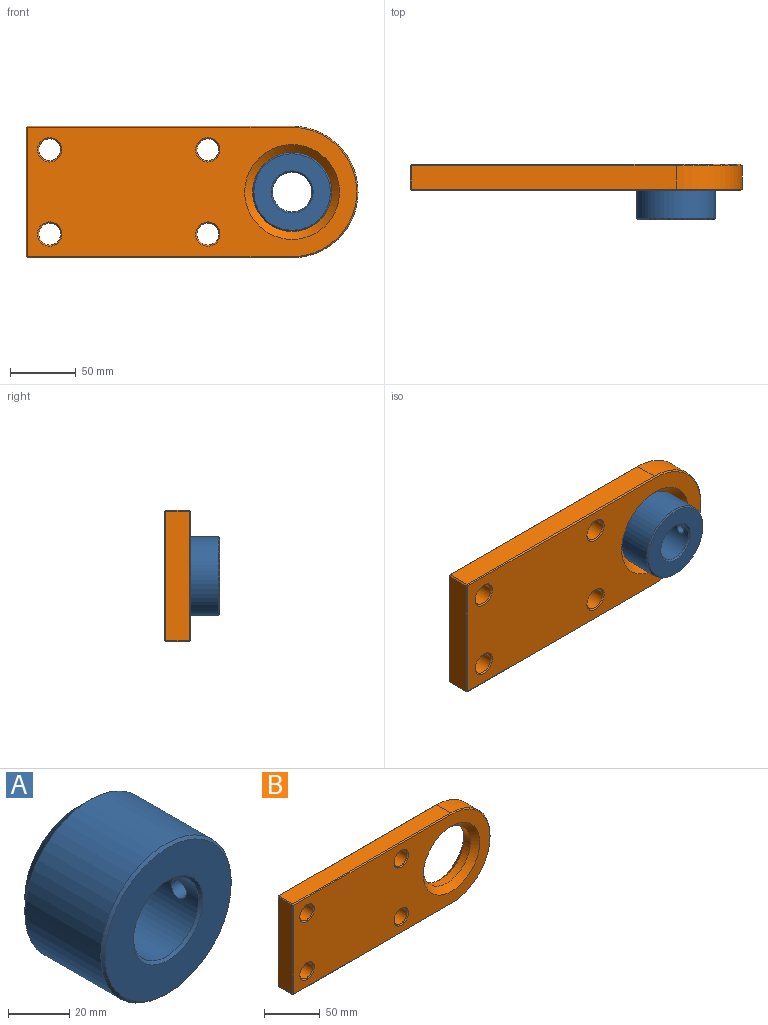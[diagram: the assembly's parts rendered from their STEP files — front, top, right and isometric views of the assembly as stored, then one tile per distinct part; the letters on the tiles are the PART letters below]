
ASSEMBLY  parts=2 mates=1
PART A: 10 faces, bbox 60x42x60 mm
  f0: cylinder r=15mm len=40mm, axis (0,1,0), area 3733.2mm2, adj f4,f6,f8
  f1: cylinder r=30mm len=60mm, axis (0,1,0), area 6538.5mm2, adj f5,f7,f9
  f2: plane 58x58mm, normal (0,-1,0), area 1837.8mm2, adj f4,f5
  f3: plane 48x48mm, normal (0,1,0), area 1005.3mm2, adj f6,f7
  f4: cone r=15mm half-angle=45deg, axis (0,-1,0), area 137.7mm2, adj f0,f2
  f5: cone r=29mm half-angle=45deg, axis (0,1,0), area 262.1mm2, adj f1,f2
  f6: cone r=16mm half-angle=45deg, axis (0,1,0), area 137.7mm2, adj f0,f3
  f7: cone r=30mm half-angle=45deg, axis (0,-1,0), area 1439.5mm2, adj f1,f3
  f8: cylinder r=3.4mm len=14.18mm, axis (-1,0,0), area 302.9mm2, adj f0,f9
  f9: bspline ~8.85x8.59mm, area 31.9mm2, adj f1,f8
PART B: 35 faces, bbox 252x20x100 mm
  f0: cylinder r=50mm len=100mm, axis (0,1,0), area 2827.4mm2, adj f1,f8,f13,f26
  f1: plane 201x18mm, normal (0,0,1), area 3618mm2, adj f0,f15,f20,f25
  f2: plane 98x18mm, normal (-1,0,0), area 1764mm2, adj f16,f19,f20,f21
  f3: cylinder r=8.25mm len=18mm, axis (0,1,0), area 933.1mm2, adj f29,f33
  f4: cylinder r=8.25mm len=18mm, axis (0,1,0), area 933.1mm2, adj f30,f34
  f5: cylinder r=8.25mm len=18mm, axis (0,1,0), area 933.1mm2, adj f28,f32
  f6: cylinder r=8.25mm len=18mm, axis (0,1,0), area 933.1mm2, adj f27,f31
  f7: cylinder r=30mm len=60mm, axis (0,1,0), area 1508mm2, adj f11,f12
  f8: plane 201x18mm, normal (0,0,-1), area 3618mm2, adj f0,f14,f19,f24
  f9: plane 250x98mm, normal (0,-1,0), area 18322.8mm2, adj f12,f13,f14,f15,f16,f31,f32,f33
  f10: plane 250x98mm, normal (0,1,0), area 18322.8mm2, adj f11,f21,f24,f25,f26,f27,f28,f29
  f11: cone r=36mm half-angle=45deg, axis (0,1,0), area 1759.4mm2, adj f7,f10
  f12: cone r=30mm half-angle=45deg, axis (0,-1,0), area 1759.4mm2, adj f7,f9
  f13: cone r=49mm half-angle=45deg, axis (0,1,0), area 219.9mm2, adj f0,f9,f14,f15
  f14: plane 201x1mm, normal (0,-0.71,-0.71), area 284.3mm2, adj f8,f9,f13,f17
  f15: plane 201x1mm, normal (0,-0.71,0.71), area 284.3mm2, adj f1,f9,f13,f18
  f16: plane 98x1mm, normal (-0.71,-0.71,0), area 138.6mm2, adj f2,f9,f17,f18
  f17: plane 1x1mm, normal (-0.58,-0.58,-0.58), area 0.9mm2, adj f14,f16,f19
  f18: plane 1x1mm, normal (-0.58,-0.58,0.58), area 0.9mm2, adj f15,f16,f20
  f19: plane 18x1mm, normal (-0.71,0,-0.71), area 25.5mm2, adj f2,f8,f17,f22
  f20: plane 18x1mm, normal (-0.71,0,0.71), area 25.5mm2, adj f1,f2,f18,f23
  f21: plane 98x1mm, normal (-0.71,0.71,0), area 138.6mm2, adj f2,f10,f22,f23
  f22: plane 1x1mm, normal (-0.58,0.58,-0.58), area 0.9mm2, adj f19,f21,f24
  f23: plane 1x1mm, normal (-0.58,0.58,0.58), area 0.9mm2, adj f20,f21,f25
  f24: plane 201x1mm, normal (0,0.71,-0.71), area 284.3mm2, adj f8,f10,f22,f26
  f25: plane 201x1mm, normal (0,0.71,0.71), area 284.3mm2, adj f1,f10,f23,f26
  f26: cone r=50mm half-angle=45deg, axis (0,-1,0), area 219.9mm2, adj f0,f10,f24,f25
  f27: cone r=9.25mm half-angle=45deg, axis (0,1,0), area 77.8mm2, adj f6,f10
  f28: cone r=9.25mm half-angle=45deg, axis (0,1,0), area 77.8mm2, adj f5,f10
  f29: cone r=9.25mm half-angle=45deg, axis (0,1,0), area 77.8mm2, adj f3,f10
  f30: cone r=9.25mm half-angle=45deg, axis (0,1,0), area 77.8mm2, adj f4,f10
  f31: cone r=8.25mm half-angle=45deg, axis (0,-1,0), area 77.8mm2, adj f6,f9
  f32: cone r=8.25mm half-angle=45deg, axis (0,-1,0), area 77.8mm2, adj f5,f9
  f33: cone r=8.25mm half-angle=45deg, axis (0,-1,0), area 77.8mm2, adj f3,f9
  f34: cone r=8.25mm half-angle=45deg, axis (0,-1,0), area 77.8mm2, adj f4,f9
PLACE A t=(67.5,22.18,25.63)mm
PLACE B t=(-8.5,22.18,25.63)mm
MATE fastened A.f0 <-> B.f7  axis (0,1,0) through (67.5,22.18,25.63)mm
